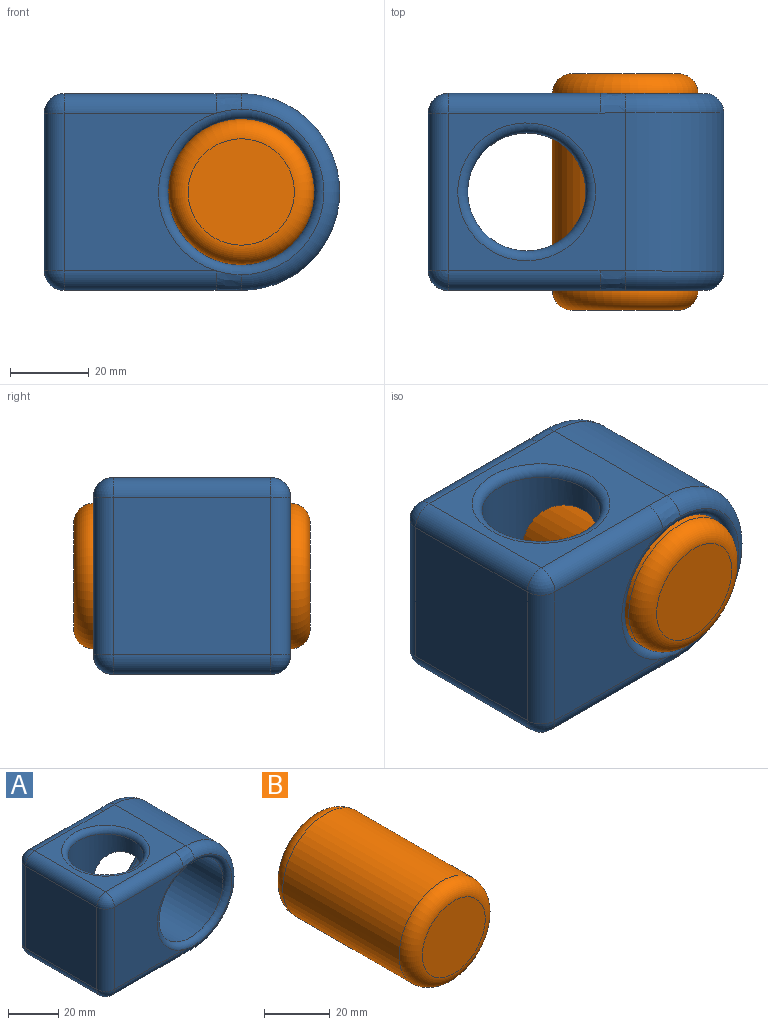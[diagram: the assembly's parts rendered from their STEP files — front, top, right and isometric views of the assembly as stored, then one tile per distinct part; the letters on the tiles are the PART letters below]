
ASSEMBLY  parts=2 mates=1
PART A: 30 faces, bbox 77.1x50.7x54.1 mm
  f0: plane 45x40.2mm, normal (0,0,1), area 838.6mm2, adj f3,f9,f12,f13,f17,f20,f23
  f1: plane 40x40mm, normal (-1,0,0), area 1600mm2, adj f17,f18,f24,f25
  f2: plane 45x40.2mm, normal (0,0,-1), area 838.6mm2, adj f3,f8,f16,f19,f25,f28,f29
  f3: cylinder r=25mm len=50mm, axis (0,1,0), area 3157.5mm2, adj f0,f2,f14,f26
  f4: plane 40x38.6mm, normal (0,-1,0), area 1115.9mm2, adj f11,f13,f18,f19
  f5: plane 40x38.6mm, normal (0,1,0), area 1115.9mm2, adj f10,f20,f24,f29
  f6: cylinder r=18.5mm len=45mm, axis (0,-1,0), area 4416.3mm2, adj f7,f10,f11
  f7: cylinder r=15mm len=45mm, axis (0,0,1), area 3398.7mm2, adj f6,f8,f9
  f8: torus R=17.5mm, axis (0,0,1), area 392.5mm2, adj f2,f7
  f9: torus R=17.5mm, axis (0,0,1), area 392.5mm2, adj f0,f7
  f10: torus R=21mm, axis (0,-1,0), area 478.9mm2, adj f5,f6,f23,f26,f28
  f11: torus R=21mm, axis (0,-1,0), area 478.9mm2, adj f4,f6,f12,f14,f16
  f12: bspline ~8.97x5.39mm, area 46mm2, adj f0,f11,f13,f14
  f13: cylinder r=5mm len=38.6mm, axis (1,0,0), area 303.1mm2, adj f0,f4,f12,f15
  f14: torus R=20mm, axis (0,-1,0), area 507.2mm2, adj f3,f11,f12,f16
  f15: sphere r=5mm, area 39.3mm2, adj f13,f17,f18
  f16: bspline ~8.97x5.39mm, area 46mm2, adj f2,f11,f14,f19
  f17: cylinder r=5mm len=40mm, axis (0,-1,0), area 314.2mm2, adj f0,f1,f15,f21
  f18: cylinder r=5mm len=40mm, axis (0,0,1), area 314.2mm2, adj f1,f4,f15,f22
  f19: cylinder r=5mm len=38.6mm, axis (-1,0,0), area 303.1mm2, adj f2,f4,f16,f22
  f20: cylinder r=5mm len=38.6mm, axis (-1,0,0), area 303.1mm2, adj f0,f5,f21,f23
  f21: sphere r=5mm, area 39.3mm2, adj f17,f20,f24
  f22: sphere r=5mm, area 39.3mm2, adj f18,f19,f25
  f23: bspline ~8.97x5.39mm, area 46mm2, adj f0,f10,f20,f26
  f24: cylinder r=5mm len=40mm, axis (0,0,-1), area 314.2mm2, adj f1,f5,f21,f27
  f25: cylinder r=5mm len=40mm, axis (0,1,0), area 314.2mm2, adj f1,f2,f22,f27
  f26: torus R=20mm, axis (0,1,0), area 507.2mm2, adj f3,f10,f23,f28
  f27: sphere r=5mm, area 39.3mm2, adj f24,f25,f29
  f28: bspline ~8.97x5.39mm, area 46mm2, adj f2,f10,f26,f29
  f29: cylinder r=5mm len=38.6mm, axis (1,0,0), area 303.1mm2, adj f2,f5,f27,f28
PART B: 5 faces, bbox 40x60x40 mm
  f0: cylinder r=18.5mm len=50mm, axis (0,1,0), area 5811.9mm2, adj f3,f4
  f1: plane 27x27mm, normal (0,-1,0), area 572.6mm2, adj f4
  f2: plane 27x27mm, normal (0,1,0), area 572.6mm2, adj f3
  f3: torus R=13.5mm, axis (0,-1,0), area 823.3mm2, adj f0,f2
  f4: torus R=13.5mm, axis (0,-1,0), area 823.3mm2, adj f0,f1
PLACE A t=(-11.87,25.37,0)mm
PLACE B t=(13.13,30.37,0)mm
MATE cylindrical B.f0 <-> A.f6  axis (0,1,0) through (13.13,0.37,0)mm
